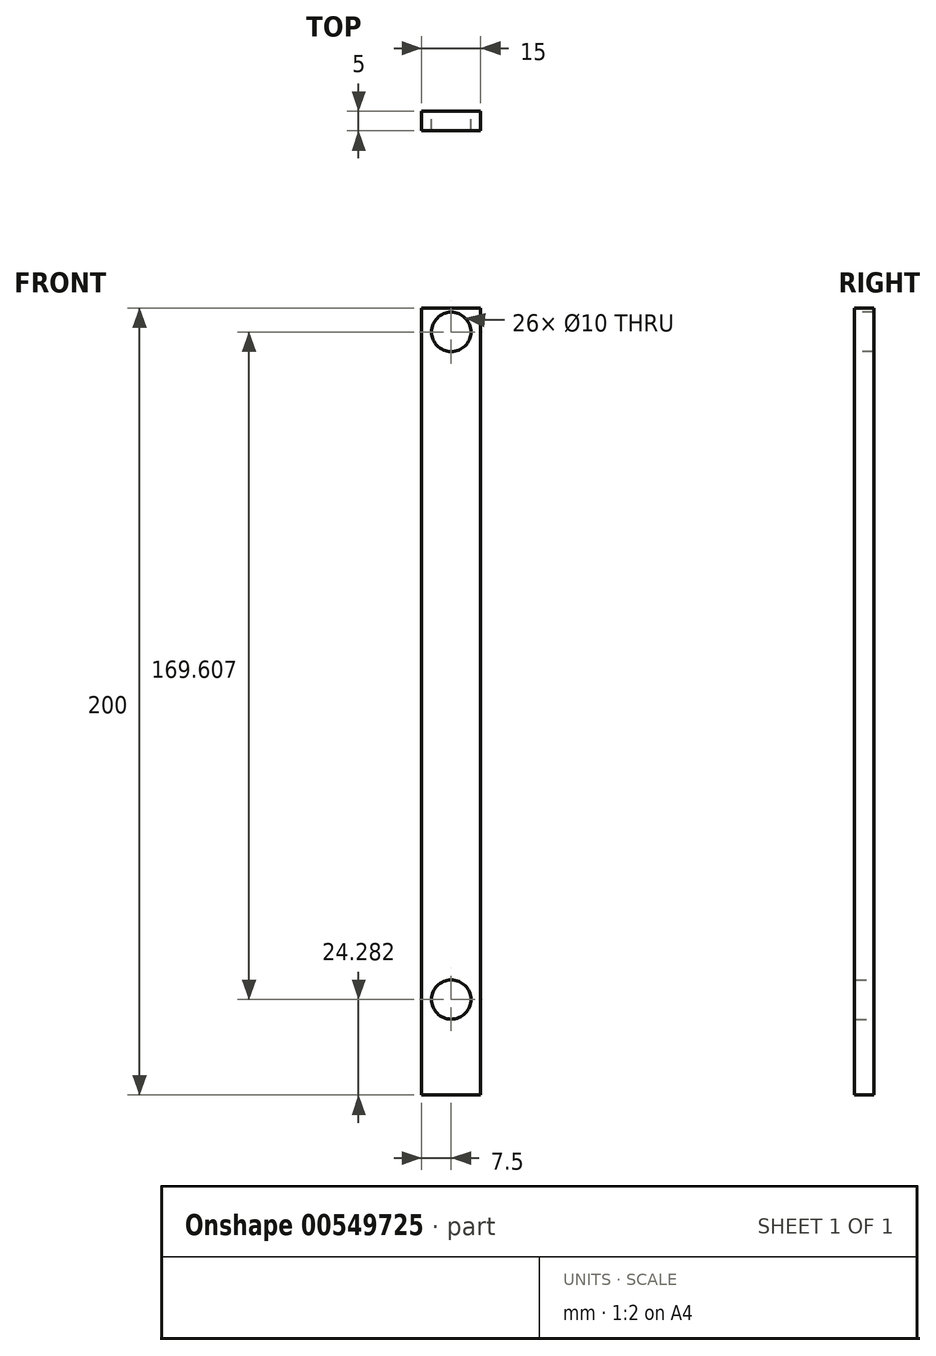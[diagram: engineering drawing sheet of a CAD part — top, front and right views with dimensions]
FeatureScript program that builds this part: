
annotation { "Feature Type Name" : "Feature", "Feature Type Description" : "" }
export const myFeature = defineFeature(function(context is Context, id is Id, definition is map)
    precondition{}
    {
        {
            var Q0;
            Q0=qCreatedBy(makeId("Front.planeOp"),FACE);
            var sketch = newSketch(context, id + "F0", { "sketchPlane" : qUnion([Q0])});
            skLineSegment(sketch, "E0.bottom", {"start": v(0, 0) * mm, "end": v(15, 0) * mm});
            skLineSegment(sketch, "E0.top", {"start": v(0, 200) * mm, "end": v(15, 200) * mm});
            skLineSegment(sketch, "E0.left", {"start": v(0, 0) * mm, "end": v(0, 200) * mm});
            skLineSegment(sketch, "E0.right", {"start": v(15, 0) * mm, "end": v(15, 200) * mm});
            skLineSegment(sketch, "E1", {"start": v(7.5, 0) * mm, "end": v(7.5, 24.28) * mm, "construction": true});
            skCircle(sketch, "E2", {"center": v(7.5, 24.28) * mm, "radius": 5 * mm});
            skSolve(sketch);
        }
        {
            var Q0;
            Q0 = qSketchRegion(id + "F0", true);
            extrude(context, id + "F1", {"entities" : qUnion([Q0]), "depth" : 5 * mm, "offsetDistance" : 25 * mm});
        }
        {
            var Q0;
            Q0=makeQuery(id+"F1.opExtrude","CAP_FACE",FACE,{"disambiguationData":[OSD([sQuery(id+"F0.wireOp",EDGE,"E0.bottom"),sQuery(id+"F0.wireOp",EDGE,"E0.top"),sQuery(id+"F0.wireOp",EDGE,"E0.left"),sQuery(id+"F0.wireOp",EDGE,"E0.right"),sQuery(id+"F0.wireOp",EDGE,"E2")])],"isStart":false});
            var sketch = newSketch(context, id + "F2", { "sketchPlane" : qUnion([Q0])});
            skLineSegment(sketch, "E3", {"start": v(7.5, 200) * mm, "end": v(7.5, 193.89) * mm, "construction": true});
            skCircle(sketch, "E4", {"center": v(7.5, 193.89) * mm, "radius": 5 * mm});
            skSolve(sketch);
        }
        {
            var Q0;
            Q0 = qSketchRegion(id + "F2", true);
            extrude(context, id + "F3", {"entities" : qUnion([Q0]), "operationType" : NewBodyOperationType.REMOVE, "endBound" : BoundingType.UP_TO_NEXT, "oppositeDirection" : true, "depth" : 25 * mm, "offsetDistance" : 25 * mm});
        }
    });
